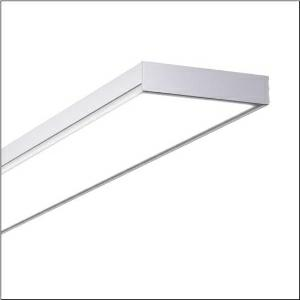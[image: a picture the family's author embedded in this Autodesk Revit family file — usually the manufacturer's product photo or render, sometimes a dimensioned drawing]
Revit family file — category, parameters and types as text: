
# Revit family: apollon_31_surface_51mp26wd2441e
name_source: partatom
category: Lighting Fixtures
units: mm (PartAtom-declared; Revit-internal decimal feet)

## family parameters
Cut with Voids When Loaded = No
Host = Face
Light Source = No
Part Type = Normal
Room Calculation Point = No
Round Connector Dimension = Use Diameter
Shared = No

## types (1)
- Apollon 31 Surface (1 x LED, 4600 lm, 33 W, 4000K)
    Apparent Load = 33 VA
    CIE Flux Codes = 61 87 97 97 100
    Color Rendering = 80
    Color Temperature = 4000K
    Default Elevation = 1800 mm
    Description = Apollon 31 Surface, office luminaire, primary optical cover: micro prismatic cover, of PMMA, light emission: direct distribution, primary light characteristic: symmetric, installation type: surface-mounted, LED, rated luminous flux: 4.600lm, luminous efficacy: 139lm/W, light colour: 840, colour temperature: 4000K, control gear: DALI 2, with terminal, 5-pole, mains connection: 220..240V, AC, 50/60Hz, rated input power: 33W, housing, of sheet steel, coated, metallic grey (RAL 9006), length: 1.545mm, width: 200mm, height: 44mm, protection rating (complete): IP20, protection rating (on room side): IP40, protection rating (lamp compartment, on room side): IP40, insulation class (complete): insulation class I (protective earthing), certification: CE, ENEC, UKCA, impact resistance: IK02, permissible operating ambient temperature: -20..+40°C, standard: EN 60598-2-22, packaging unit: 1 piece
    Height = 44 mm
    Lamp = 1 x LED
    Lamp Light Flux = 4600 lm
    Lamp Power = 33 W
    Lamp count = 1
    Length = 1545 mm
    Luminous efficacy = 139 lm/W
    Manufacturer = Siteco
    ModVariant = No
    Model = 51MP26WD2441E
    Mounting Place = Ceiling
    Mounting Type = Surface mounted
    Number of Poles = 1
    OnlyDefault = Yes
    Power Factor = 1
    Product Name = Apollon 31 Surface
    Product group = office luminaire | ceiling mounted
    ProductGroupID = 301
    Protection Class = Protection class I
    Protection Degree = IP 20
    RLX_Detail_Level = 1
    RLX_Emergency_Light_Flux = 0 lm
    RLX_Emergency_Type = 0
    RLX_Emergency_Type_DB = No
    RlxData = <blob elided: 24145 chars, md5=6e2c3684>
    Socket = socket
    Standby Power = 0 W
    System Light Flux = 4600 lm
    System Power = 33 W
    Type Comments = Product without accessories
    Type Image = l_1313654.jpg
    URL = http://relux.com
    VarID = ---
    Voltage = 0 V
    Weight = 0.00 kg
    Width = 200 mm  [stored 0.656168 ft]

note: [stored X ft] marks values corroborated as IEEE doubles in the binary element streams (Revit-internal decimal feet)

## geometry (parser evidence)
native form markers: Blend x4, Sweep x11
no freeform markers — native parametric forms only
